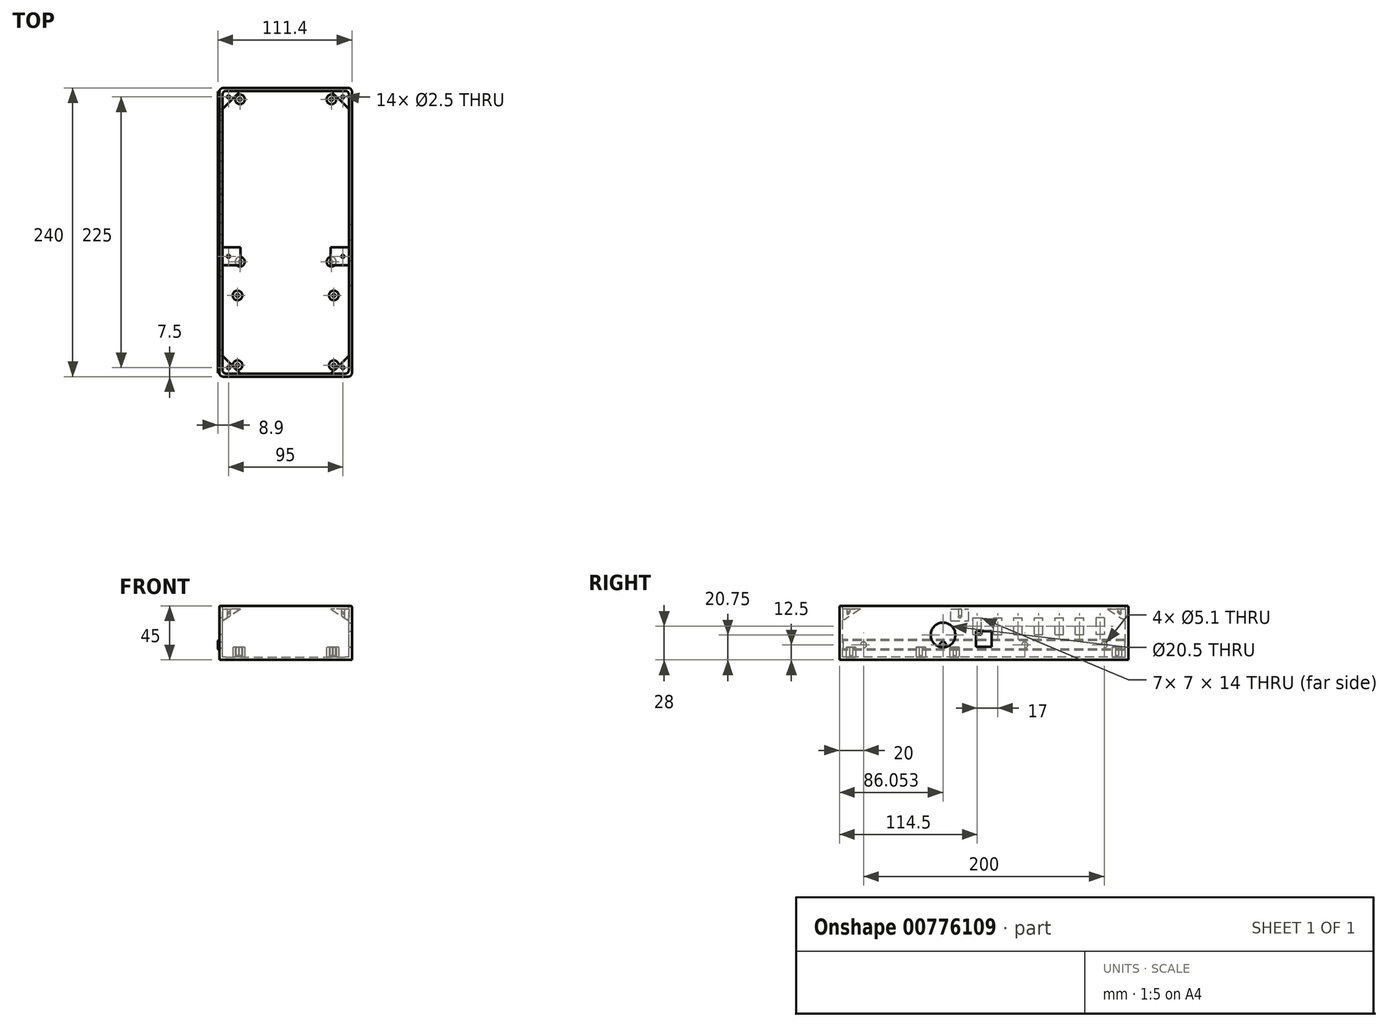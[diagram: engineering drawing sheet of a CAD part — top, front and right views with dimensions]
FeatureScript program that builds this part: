
annotation { "Feature Type Name" : "Feature", "Feature Type Description" : "" }
export const myFeature = defineFeature(function(context is Context, id is Id, definition is map)
    precondition{}
    {
        {
            var Q0;
            Q0=qCreatedBy(makeId("Top.planeOp"),FACE);
            var sketch = newSketch(context, id + "F0", { "sketchPlane" : qUnion([Q0])});
            skLineSegment(sketch, "E0.bottom", {"start": v(55, -120) * mm, "end": v(-55, -120) * mm});
            skLineSegment(sketch, "E0.top", {"start": v(55, 120) * mm, "end": v(-55, 120) * mm});
            skLineSegment(sketch, "E0.left", {"start": v(55, -120) * mm, "end": v(55, 120) * mm});
            skLineSegment(sketch, "E0.right", {"start": v(-55, -120) * mm, "end": v(-55, 120) * mm});
            skPoint(sketch, "E0.middle", {"position": v(0, 0) * mm});
            skSolve(sketch);
        }
        {
            var Q0;
            Q0=makeQuery(id+"F0.imprint","IMPRINT",FACE,{"disambiguationData":[TD([[makeQuery(id+"F0.imprint","IMPRINT",EDGE,{"derivedFrom":sQuery(id+"F0.wireOp",EDGE,"E0.bottom")}),-1.0]])]});
            extrude(context, id + "F1", {"entities" : qUnion([Q0]), "depth" : 45 * mm, "offsetDistance" : 25 * mm});
        }
        {
            var Q0;
            Q0=makeQuery(id+"F1.opExtrude","CAP_FACE",FACE,{"disambiguationData":[OSD([sQuery(id+"F0.wireOp",EDGE,"E0.bottom"),sQuery(id+"F0.wireOp",EDGE,"E0.top"),sQuery(id+"F0.wireOp",EDGE,"E0.left"),sQuery(id+"F0.wireOp",EDGE,"E0.right")])],"isStart":false});
            var sketch = newSketch(context, id + "F2", { "sketchPlane" : qUnion([Q0])});
            skLineSegment(sketch, "E1.bottom", {"start": v(52.5, -117.5) * mm, "end": v(-52.5, -117.5) * mm});
            skLineSegment(sketch, "E1.top", {"start": v(52.5, 117.5) * mm, "end": v(-52.5, 117.5) * mm});
            skLineSegment(sketch, "E1.left", {"start": v(52.5, -117.5) * mm, "end": v(52.5, 117.5) * mm});
            skLineSegment(sketch, "E1.right", {"start": v(-52.5, -117.5) * mm, "end": v(-52.5, 117.5) * mm});
            skPoint(sketch, "E1.middle", {"position": v(0, 0) * mm});
            skSolve(sketch);
        }
        {
            var Q0;
            Q0=qSketchRegion(id+"F2",true);
            var Q1;
            Q1=makeQuery(id+"F1.opExtrude","CAP_FACE",FACE,{"disambiguationData":[OSD([sQuery(id+"F0.wireOp",EDGE,"E0.bottom"),sQuery(id+"F0.wireOp",EDGE,"E0.top"),sQuery(id+"F0.wireOp",EDGE,"E0.left"),sQuery(id+"F0.wireOp",EDGE,"E0.right")])],"isStart":true});
            extrude(context, id + "F3", {"entities" : qUnion([Q0]), "operationType" : NewBodyOperationType.REMOVE, "endBound" : BoundingType.UP_TO_SURFACE, "oppositeDirection" : true, "depth" : 35 * mm, "endBoundEntityFace" : qUnion([Q1]), "hasOffset" : true, "offsetDistance" : 2.5 * mm});
        }
        {
            var Q0;
            Q0=makeQuery(id+"F3.boolean.opBoolean","COPY",FACE,{"derivedFrom":makeQuery(id+"F3.opExtrude","CAP_FACE",FACE,{"disambiguationData":[OSD([sQuery(id+"F2.wireOp",EDGE,"E1.bottom"),sQuery(id+"F2.wireOp",EDGE,"E1.top"),sQuery(id+"F2.wireOp",EDGE,"E1.left"),sQuery(id+"F2.wireOp",EDGE,"E1.right")])],"isStart":false})});
            var sketch = newSketch(context, id + "F4", { "sketchPlane" : qUnion([Q0])});
            skCircle(sketch, "E2", {"center": v(-38, 110.5) * mm, "radius": 4 * mm});
            skCircle(sketch, "E3", {"center": v(38, 110.5) * mm, "radius": 4 * mm});
            skCircle(sketch, "E4", {"center": v(-38, -24.5) * mm, "radius": 4 * mm});
            skCircle(sketch, "E5", {"center": v(38, -24.5) * mm, "radius": 4 * mm});
            skCircle(sketch, "E6", {"center": v(-40, -52.5) * mm, "radius": 4 * mm});
            skCircle(sketch, "E7", {"center": v(40, -52.5) * mm, "radius": 4 * mm});
            skCircle(sketch, "E8", {"center": v(-40, -110.5) * mm, "radius": 4 * mm});
            skCircle(sketch, "E9", {"center": v(40, -110.5) * mm, "radius": 4 * mm});
            skSolve(sketch);
        }
        {
            var Q0;
            Q0=makeQuery(id+"F4.imprint","IMPRINT",FACE,{"disambiguationData":[TD([[makeQuery(id+"F4.imprint","IMPRINT",EDGE,{"derivedFrom":sQuery(id+"F4.wireOp",EDGE,"E2")}),1.0]])]});
            var Q1;
            Q1=makeQuery(id+"F4.imprint","IMPRINT",FACE,{"disambiguationData":[TD([[makeQuery(id+"F4.imprint","IMPRINT",EDGE,{"derivedFrom":sQuery(id+"F4.wireOp",EDGE,"E3")}),1.0]])]});
            var Q2;
            Q2=makeQuery(id+"F4.imprint","IMPRINT",FACE,{"disambiguationData":[TD([[makeQuery(id+"F4.imprint","IMPRINT",EDGE,{"derivedFrom":sQuery(id+"F4.wireOp",EDGE,"E4")}),1.0]])]});
            var Q3;
            Q3=makeQuery(id+"F4.imprint","IMPRINT",FACE,{"disambiguationData":[TD([[makeQuery(id+"F4.imprint","IMPRINT",EDGE,{"derivedFrom":sQuery(id+"F4.wireOp",EDGE,"E5")}),1.0]])]});
            var Q4;
            Q4=makeQuery(id+"F4.imprint","IMPRINT",FACE,{"disambiguationData":[TD([[makeQuery(id+"F4.imprint","IMPRINT",EDGE,{"derivedFrom":sQuery(id+"F4.wireOp",EDGE,"E6")}),1.0]])]});
            var Q5;
            Q5=makeQuery(id+"F4.imprint","IMPRINT",FACE,{"disambiguationData":[TD([[makeQuery(id+"F4.imprint","IMPRINT",EDGE,{"derivedFrom":sQuery(id+"F4.wireOp",EDGE,"E7")}),1.0]])]});
            var Q6;
            Q6=makeQuery(id+"F4.imprint","IMPRINT",FACE,{"disambiguationData":[TD([[makeQuery(id+"F4.imprint","IMPRINT",EDGE,{"derivedFrom":sQuery(id+"F4.wireOp",EDGE,"E8")}),1.0]])]});
            var Q7;
            Q7=makeQuery(id+"F4.imprint","IMPRINT",FACE,{"disambiguationData":[TD([[makeQuery(id+"F4.imprint","IMPRINT",EDGE,{"derivedFrom":sQuery(id+"F4.wireOp",EDGE,"E9")}),1.0]])]});
            extrude(context, id + "F5", {"entities" : qUnion([Q0, Q1, Q2, Q3, Q4, Q5, Q6, Q7]), "operationType" : NewBodyOperationType.ADD, "depth" : 8 * mm, "offsetDistance" : 25 * mm});
        }
        {
            var Q0;
            Q0=makeQuery(id+"F1.opExtrude","SWEPT_FACE",FACE,{"disambiguationData":[OSD([sQuery(id+"F0.wireOp",EDGE,"E0.left")])]});
            var sketch = newSketch(context, id + "F6", { "sketchPlane" : qUnion([Q0])});
            skLineSegment(sketch, "E10.bottom", {"start": v(-6.5, 24) * mm, "end": v(6.5, 24) * mm});
            skLineSegment(sketch, "E10.top", {"start": v(-6.5, 11) * mm, "end": v(6.5, 11) * mm});
            skLineSegment(sketch, "E10.left", {"start": v(-6.5, 24) * mm, "end": v(-6.5, 11) * mm});
            skLineSegment(sketch, "E10.right", {"start": v(6.5, 24) * mm, "end": v(6.5, 11) * mm});
            skPoint(sketch, "E11.0", {"position": v(-24.5, 2.5) * mm});
            skLineSegment(sketch, "E12.0.0", {"start": v(-28.5, 10.5) * mm, "end": v(-20.5, 10.5) * mm});
            skSolve(sketch);
        }
        {
            var Q0;
            Q0=makeQuery(id+"F6.imprint","IMPRINT",FACE,{"disambiguationData":[TD([[makeQuery(id+"F6.imprint","IMPRINT",EDGE,{"derivedFrom":sQuery(id+"F6.wireOp",EDGE,"E10.bottom")}),-1.0]])]});
            var Q1;
            Q1=makeQuery(id+"F3.boolean.opBoolean","COPY",FACE,{"derivedFrom":makeQuery(id+"F3.opExtrude","SWEPT_FACE",FACE,{"disambiguationData":[OSD([sQuery(id+"F2.wireOp",EDGE,"E1.left")])]})});
            extrude(context, id + "F7", {"entities" : qUnion([Q0]), "operationType" : NewBodyOperationType.REMOVE, "endBound" : BoundingType.UP_TO_SURFACE, "oppositeDirection" : true, "depth" : 25 * mm, "endBoundEntityFace" : qUnion([Q1]), "offsetDistance" : 25 * mm});
        }
        {
            var Q0;
            Q0=makeQuery(id+"F1.opExtrude","SWEPT_FACE",FACE,{"disambiguationData":[OSD([sQuery(id+"F0.wireOp",EDGE,"E0.right")])]});
            var sketch = newSketch(context, id + "F8", { "sketchPlane" : qUnion([Q0])});
            skLineSegment(sketch, "E13.bottom", {"start": v(-100, 35) * mm, "end": v(-93, 35) * mm});
            skLineSegment(sketch, "E13.top", {"start": v(-100, 21) * mm, "end": v(-93, 21) * mm});
            skLineSegment(sketch, "E13.left", {"start": v(-100, 35) * mm, "end": v(-100, 21) * mm});
            skLineSegment(sketch, "E13.right", {"start": v(-93, 35) * mm, "end": v(-93, 21) * mm});
            skLineSegment(sketch, "E14.bottom", {"start": v(-76, 21) * mm, "end": v(-83, 21) * mm});
            skLineSegment(sketch, "E14.top", {"start": v(-76, 35) * mm, "end": v(-83, 35) * mm});
            skLineSegment(sketch, "E14.left", {"start": v(-76, 21) * mm, "end": v(-76, 35) * mm});
            skLineSegment(sketch, "E14.right", {"start": v(-83, 21) * mm, "end": v(-83, 35) * mm});
            skPoint(sketch, "E14.middle", {"position": v(-79.5, 28) * mm});
            skLineSegment(sketch, "E15.bottom", {"start": v(-59, 21) * mm, "end": v(-66, 21) * mm});
            skLineSegment(sketch, "E15.top", {"start": v(-59, 35) * mm, "end": v(-66, 35) * mm});
            skLineSegment(sketch, "E15.left", {"start": v(-59, 21) * mm, "end": v(-59, 35) * mm});
            skLineSegment(sketch, "E15.right", {"start": v(-66, 21) * mm, "end": v(-66, 35) * mm});
            skPoint(sketch, "E15.middle", {"position": v(-62.5, 28) * mm});
            skLineSegment(sketch, "E16.bottom", {"start": v(-42, 21) * mm, "end": v(-49, 21) * mm});
            skLineSegment(sketch, "E16.top", {"start": v(-42, 35) * mm, "end": v(-49, 35) * mm});
            skLineSegment(sketch, "E16.left", {"start": v(-42, 21) * mm, "end": v(-42, 35) * mm});
            skLineSegment(sketch, "E16.right", {"start": v(-49, 21) * mm, "end": v(-49, 35) * mm});
            skPoint(sketch, "E16.middle", {"position": v(-45.5, 28) * mm});
            skLineSegment(sketch, "E17.bottom", {"start": v(9, 21) * mm, "end": v(2, 21) * mm});
            skLineSegment(sketch, "E17.top", {"start": v(9, 35) * mm, "end": v(2, 35) * mm});
            skLineSegment(sketch, "E17.left", {"start": v(9, 21) * mm, "end": v(9, 35) * mm});
            skLineSegment(sketch, "E17.right", {"start": v(2, 21) * mm, "end": v(2, 35) * mm});
            skPoint(sketch, "E17.middle", {"position": v(5.5, 28) * mm});
            skLineSegment(sketch, "E18.bottom", {"start": v(-8, 21) * mm, "end": v(-15, 21) * mm});
            skLineSegment(sketch, "E18.top", {"start": v(-8, 35) * mm, "end": v(-15, 35) * mm});
            skLineSegment(sketch, "E18.left", {"start": v(-8, 21) * mm, "end": v(-8, 35) * mm});
            skLineSegment(sketch, "E18.right", {"start": v(-15, 21) * mm, "end": v(-15, 35) * mm});
            skPoint(sketch, "E18.middle", {"position": v(-11.5, 28) * mm});
            skLineSegment(sketch, "E19.bottom", {"start": v(-25, 21) * mm, "end": v(-32, 21) * mm});
            skLineSegment(sketch, "E19.top", {"start": v(-25, 35) * mm, "end": v(-32, 35) * mm});
            skLineSegment(sketch, "E19.left", {"start": v(-25, 21) * mm, "end": v(-25, 35) * mm});
            skLineSegment(sketch, "E19.right", {"start": v(-32, 21) * mm, "end": v(-32, 35) * mm});
            skPoint(sketch, "E19.middle", {"position": v(-28.5, 28) * mm});
            skSolve(sketch);
        }
        {
            var Q0;
            Q0=makeQuery(id+"F8.imprint","IMPRINT",FACE,{"disambiguationData":[TD([[makeQuery(id+"F8.imprint","IMPRINT",EDGE,{"derivedFrom":sQuery(id+"F8.wireOp",EDGE,"E15.bottom")}),-1.0]])]});
            var Q1;
            Q1=makeQuery(id+"F8.imprint","IMPRINT",FACE,{"disambiguationData":[TD([[makeQuery(id+"F8.imprint","IMPRINT",EDGE,{"derivedFrom":sQuery(id+"F8.wireOp",EDGE,"E16.bottom")}),-1.0]])]});
            var Q2;
            Q2=makeQuery(id+"F8.imprint","IMPRINT",FACE,{"disambiguationData":[TD([[makeQuery(id+"F8.imprint","IMPRINT",EDGE,{"derivedFrom":sQuery(id+"F8.wireOp",EDGE,"E19.bottom")}),-1.0]])]});
            var Q3;
            Q3=makeQuery(id+"F8.imprint","IMPRINT",FACE,{"disambiguationData":[TD([[makeQuery(id+"F8.imprint","IMPRINT",EDGE,{"derivedFrom":sQuery(id+"F8.wireOp",EDGE,"E18.bottom")}),-1.0]])]});
            var Q4;
            Q4=makeQuery(id+"F8.imprint","IMPRINT",FACE,{"disambiguationData":[TD([[makeQuery(id+"F8.imprint","IMPRINT",EDGE,{"derivedFrom":sQuery(id+"F8.wireOp",EDGE,"E17.bottom")}),-1.0]])]});
            var Q5;
            Q5=makeQuery(id+"F8.imprint","IMPRINT",FACE,{"disambiguationData":[TD([[makeQuery(id+"F8.imprint","IMPRINT",EDGE,{"derivedFrom":sQuery(id+"F8.wireOp",EDGE,"E14.bottom")}),-1.0]])]});
            var Q6;
            Q6=makeQuery(id+"F8.imprint","IMPRINT",FACE,{"disambiguationData":[TD([[makeQuery(id+"F8.imprint","IMPRINT",EDGE,{"derivedFrom":sQuery(id+"F8.wireOp",EDGE,"E13.bottom")}),-1.0]])]});
            var Q7;
            Q7=makeQuery(id+"F3.boolean.opBoolean","COPY",FACE,{"derivedFrom":makeQuery(id+"F3.opExtrude","SWEPT_FACE",FACE,{"disambiguationData":[OSD([sQuery(id+"F2.wireOp",EDGE,"E1.right")])]})});
            extrude(context, id + "F9", {"entities" : qUnion([Q0, Q1, Q2, Q3, Q4, Q5, Q6]), "operationType" : NewBodyOperationType.REMOVE, "endBound" : BoundingType.UP_TO_SURFACE, "oppositeDirection" : true, "depth" : 25 * mm, "endBoundEntityFace" : qUnion([Q7]), "offsetDistance" : 25 * mm});
        }
        {
            var Q0;
            Q0=makeQuery(id+"F1.opExtrude","SWEPT_EDGE",EDGE,{"disambiguationData":[OSD([sQuery(id+"F0.wireOp",EDGE,"E0.bottom"),sQuery(id+"F0.wireOp",EDGE,"E0.right")])]});
            var Q1;
            Q1=makeQuery(id+"F1.opExtrude","SWEPT_EDGE",EDGE,{"disambiguationData":[OSD([sQuery(id+"F0.wireOp",EDGE,"E0.bottom"),sQuery(id+"F0.wireOp",EDGE,"E0.left")])]});
            var Q2;
            Q2=makeQuery(id+"F1.opExtrude","SWEPT_EDGE",EDGE,{"disambiguationData":[OSD([sQuery(id+"F0.wireOp",EDGE,"E0.top"),sQuery(id+"F0.wireOp",EDGE,"E0.right")])]});
            var Q3;
            Q3=makeQuery(id+"F1.opExtrude","SWEPT_EDGE",EDGE,{"disambiguationData":[OSD([sQuery(id+"F0.wireOp",EDGE,"E0.top"),sQuery(id+"F0.wireOp",EDGE,"E0.left")])]});
            fillet(context, id + "F10", {"entities" : qUnion([Q0, Q1, Q2, Q3]), "radius" : 3 * mm, "tangentPropagation" : true, "allowEdgeOverflow" : false});
        }
        {
            var Q0;
            Q0=makeQuery(id+"F3.boolean.opBoolean","COPY",EDGE,{"derivedFrom":makeQuery(id+"F3.opExtrude","SWEPT_EDGE",EDGE,{"disambiguationData":[OSD([sQuery(id+"F2.wireOp",EDGE,"E1.bottom"),sQuery(id+"F2.wireOp",EDGE,"E1.right")])]})});
            var Q1;
            Q1=makeQuery(id+"F3.boolean.opBoolean","COPY",EDGE,{"derivedFrom":makeQuery(id+"F3.opExtrude","SWEPT_EDGE",EDGE,{"disambiguationData":[OSD([sQuery(id+"F2.wireOp",EDGE,"E1.bottom"),sQuery(id+"F2.wireOp",EDGE,"E1.left")])]})});
            var Q2;
            Q2=makeQuery(id+"F3.boolean.opBoolean","COPY",EDGE,{"derivedFrom":makeQuery(id+"F3.opExtrude","SWEPT_EDGE",EDGE,{"disambiguationData":[OSD([sQuery(id+"F2.wireOp",EDGE,"E1.top"),sQuery(id+"F2.wireOp",EDGE,"E1.right")])]})});
            var Q3;
            Q3=makeQuery(id+"F3.boolean.opBoolean","COPY",EDGE,{"derivedFrom":makeQuery(id+"F3.opExtrude","SWEPT_EDGE",EDGE,{"disambiguationData":[OSD([sQuery(id+"F2.wireOp",EDGE,"E1.top"),sQuery(id+"F2.wireOp",EDGE,"E1.left")])]})});
            fillet(context, id + "F11", {"entities" : qUnion([Q0, Q1, Q2, Q3]), "radius" : 3 * mm, "tangentPropagation" : true, "allowEdgeOverflow" : false});
        }
        {
            var Q0;
            Q0=makeQuery(id+"F1.opExtrude","SWEPT_FACE",FACE,{"disambiguationData":[OSD([sQuery(id+"F0.wireOp",EDGE,"E0.left")])]});
            var sketch = newSketch(context, id + "F12", { "sketchPlane" : qUnion([Q0])});
            skCircle(sketch, "E20", {"center": v(-33.95, 20.75) * mm, "radius": 10.25 * mm});
            skLineSegment(sketch, "E21.0", {"start": v(-56.5, 10.5) * mm, "end": v(-48.5, 10.5) * mm});
            skLineSegment(sketch, "E22", {"start": v(-52.5, 10.5) * mm, "end": v(-13.25, 10.5) * mm});
            skSolve(sketch);
        }
        {
            var Q0;
            Q0=makeQuery(id+"F12.imprint","IMPRINT",FACE,{"disambiguationData":[TD([[makeQuery(id+"F12.imprint","IMPRINT",EDGE,{"derivedFrom":sQuery(id+"F12.wireOp",EDGE,"E20")}),1.0]])]});
            var Q1;
            Q1=makeQuery(id+"F3.boolean.opBoolean","COPY",FACE,{"derivedFrom":makeQuery(id+"F3.opExtrude","SWEPT_FACE",FACE,{"disambiguationData":[OSD([sQuery(id+"F2.wireOp",EDGE,"E1.left")])]})});
            extrude(context, id + "F13", {"entities" : qUnion([Q0]), "operationType" : NewBodyOperationType.REMOVE, "endBound" : BoundingType.UP_TO_SURFACE, "oppositeDirection" : true, "depth" : 25 * mm, "endBoundEntityFace" : qUnion([Q1]), "offsetDistance" : 25 * mm});
        }
        {
            var Q0;
            Q0=makeQuery(id+"F1.opExtrude","CAP_EDGE",EDGE,{"disambiguationData":[OSD([sQuery(id+"F0.wireOp",EDGE,"E0.bottom")])],"isStart":false});
            var Q1;
            Q1=makeQuery(id+"F13.boolean.opBoolean","COPY",EDGE,{"derivedFrom":makeQuery(id+"F13.opExtrude","CAP_EDGE",EDGE,{"disambiguationData":[OSD([sQuery(id+"F12.wireOp",EDGE,"E20")])],"isStart":true})});
            var Q2;
            Q2=makeQuery(id+"F7.boolean.opBoolean","COPY",EDGE,{"derivedFrom":makeQuery(id+"F7.opExtrude","CAP_EDGE",EDGE,{"disambiguationData":[OSD([sQuery(id+"F6.wireOp",EDGE,"E10.left")])],"isStart":true})});
            var Q3;
            Q3=makeQuery(id+"F7.boolean.opBoolean","COPY",EDGE,{"derivedFrom":makeQuery(id+"F7.opExtrude","CAP_EDGE",EDGE,{"disambiguationData":[OSD([sQuery(id+"F6.wireOp",EDGE,"E10.top")])],"isStart":true})});
            var Q4;
            Q4=makeQuery(id+"F7.boolean.opBoolean","COPY",EDGE,{"derivedFrom":makeQuery(id+"F7.opExtrude","CAP_EDGE",EDGE,{"disambiguationData":[OSD([sQuery(id+"F6.wireOp",EDGE,"E10.right")])],"isStart":true})});
            var Q5;
            Q5=makeQuery(id+"F7.boolean.opBoolean","COPY",EDGE,{"derivedFrom":makeQuery(id+"F7.opExtrude","CAP_EDGE",EDGE,{"disambiguationData":[OSD([sQuery(id+"F6.wireOp",EDGE,"E10.bottom")])],"isStart":true})});
            var Q6;
            Q6=makeQuery(id+"F9.boolean.opBoolean","COPY",EDGE,{"derivedFrom":makeQuery(id+"F9.opExtrude","CAP_EDGE",EDGE,{"disambiguationData":[OSD([sQuery(id+"F8.wireOp",EDGE,"E13.left")])],"isStart":true})});
            var Q7;
            Q7=makeQuery(id+"F9.boolean.opBoolean","COPY",EDGE,{"derivedFrom":makeQuery(id+"F9.opExtrude","CAP_EDGE",EDGE,{"disambiguationData":[OSD([sQuery(id+"F8.wireOp",EDGE,"E13.right")])],"isStart":true})});
            var Q8;
            Q8=makeQuery(id+"F9.boolean.opBoolean","COPY",EDGE,{"derivedFrom":makeQuery(id+"F9.opExtrude","CAP_EDGE",EDGE,{"disambiguationData":[OSD([sQuery(id+"F8.wireOp",EDGE,"E13.top")])],"isStart":true})});
            var Q9;
            Q9=makeQuery(id+"F9.boolean.opBoolean","COPY",EDGE,{"derivedFrom":makeQuery(id+"F9.opExtrude","CAP_EDGE",EDGE,{"disambiguationData":[OSD([sQuery(id+"F8.wireOp",EDGE,"E13.bottom")])],"isStart":true})});
            var Q10;
            Q10=makeQuery(id+"F9.boolean.opBoolean","COPY",EDGE,{"derivedFrom":makeQuery(id+"F9.opExtrude","CAP_EDGE",EDGE,{"disambiguationData":[OSD([sQuery(id+"F8.wireOp",EDGE,"E14.top")])],"isStart":true})});
            var Q11;
            Q11=makeQuery(id+"F9.boolean.opBoolean","COPY",EDGE,{"derivedFrom":makeQuery(id+"F9.opExtrude","CAP_EDGE",EDGE,{"disambiguationData":[OSD([sQuery(id+"F8.wireOp",EDGE,"E14.right")])],"isStart":true})});
            var Q12;
            Q12=makeQuery(id+"F9.boolean.opBoolean","COPY",EDGE,{"derivedFrom":makeQuery(id+"F9.opExtrude","CAP_EDGE",EDGE,{"disambiguationData":[OSD([sQuery(id+"F8.wireOp",EDGE,"E14.bottom")])],"isStart":true})});
            var Q13;
            Q13=makeQuery(id+"F9.boolean.opBoolean","COPY",EDGE,{"derivedFrom":makeQuery(id+"F9.opExtrude","CAP_EDGE",EDGE,{"disambiguationData":[OSD([sQuery(id+"F8.wireOp",EDGE,"E14.left")])],"isStart":true})});
            var Q14;
            Q14=makeQuery(id+"F9.boolean.opBoolean","COPY",EDGE,{"derivedFrom":makeQuery(id+"F9.opExtrude","CAP_EDGE",EDGE,{"disambiguationData":[OSD([sQuery(id+"F8.wireOp",EDGE,"E15.top")])],"isStart":true})});
            var Q15;
            Q15=makeQuery(id+"F9.boolean.opBoolean","COPY",EDGE,{"derivedFrom":makeQuery(id+"F9.opExtrude","CAP_EDGE",EDGE,{"disambiguationData":[OSD([sQuery(id+"F8.wireOp",EDGE,"E15.right")])],"isStart":true})});
            var Q16;
            Q16=makeQuery(id+"F9.boolean.opBoolean","COPY",EDGE,{"derivedFrom":makeQuery(id+"F9.opExtrude","CAP_EDGE",EDGE,{"disambiguationData":[OSD([sQuery(id+"F8.wireOp",EDGE,"E15.bottom")])],"isStart":true})});
            var Q17;
            Q17=makeQuery(id+"F9.boolean.opBoolean","COPY",EDGE,{"derivedFrom":makeQuery(id+"F9.opExtrude","CAP_EDGE",EDGE,{"disambiguationData":[OSD([sQuery(id+"F8.wireOp",EDGE,"E15.left")])],"isStart":true})});
            var Q18;
            Q18=makeQuery(id+"F9.boolean.opBoolean","COPY",EDGE,{"derivedFrom":makeQuery(id+"F9.opExtrude","CAP_EDGE",EDGE,{"disambiguationData":[OSD([sQuery(id+"F8.wireOp",EDGE,"E16.top")])],"isStart":true})});
            var Q19;
            Q19=makeQuery(id+"F9.boolean.opBoolean","COPY",EDGE,{"derivedFrom":makeQuery(id+"F9.opExtrude","CAP_EDGE",EDGE,{"disambiguationData":[OSD([sQuery(id+"F8.wireOp",EDGE,"E16.left")])],"isStart":true})});
            var Q20;
            Q20=makeQuery(id+"F9.boolean.opBoolean","COPY",EDGE,{"derivedFrom":makeQuery(id+"F9.opExtrude","CAP_EDGE",EDGE,{"disambiguationData":[OSD([sQuery(id+"F8.wireOp",EDGE,"E16.right")])],"isStart":true})});
            var Q21;
            Q21=makeQuery(id+"F9.boolean.opBoolean","COPY",EDGE,{"derivedFrom":makeQuery(id+"F9.opExtrude","CAP_EDGE",EDGE,{"disambiguationData":[OSD([sQuery(id+"F8.wireOp",EDGE,"E16.bottom")])],"isStart":true})});
            var Q22;
            Q22=makeQuery(id+"F9.boolean.opBoolean","COPY",EDGE,{"derivedFrom":makeQuery(id+"F9.opExtrude","CAP_EDGE",EDGE,{"disambiguationData":[OSD([sQuery(id+"F8.wireOp",EDGE,"E19.right")])],"isStart":true})});
            var Q23;
            Q23=makeQuery(id+"F9.boolean.opBoolean","COPY",EDGE,{"derivedFrom":makeQuery(id+"F9.opExtrude","CAP_EDGE",EDGE,{"disambiguationData":[OSD([sQuery(id+"F8.wireOp",EDGE,"E19.bottom")])],"isStart":true})});
            var Q24;
            Q24=makeQuery(id+"F9.boolean.opBoolean","COPY",EDGE,{"derivedFrom":makeQuery(id+"F9.opExtrude","CAP_EDGE",EDGE,{"disambiguationData":[OSD([sQuery(id+"F8.wireOp",EDGE,"E19.top")])],"isStart":true})});
            var Q25;
            Q25=makeQuery(id+"F9.boolean.opBoolean","COPY",EDGE,{"derivedFrom":makeQuery(id+"F9.opExtrude","CAP_EDGE",EDGE,{"disambiguationData":[OSD([sQuery(id+"F8.wireOp",EDGE,"E19.left")])],"isStart":true})});
            var Q26;
            Q26=makeQuery(id+"F9.boolean.opBoolean","COPY",EDGE,{"derivedFrom":makeQuery(id+"F9.opExtrude","CAP_EDGE",EDGE,{"disambiguationData":[OSD([sQuery(id+"F8.wireOp",EDGE,"E18.right")])],"isStart":true})});
            var Q27;
            Q27=makeQuery(id+"F9.boolean.opBoolean","COPY",EDGE,{"derivedFrom":makeQuery(id+"F9.opExtrude","CAP_EDGE",EDGE,{"disambiguationData":[OSD([sQuery(id+"F8.wireOp",EDGE,"E18.bottom")])],"isStart":true})});
            var Q28;
            Q28=makeQuery(id+"F9.boolean.opBoolean","COPY",EDGE,{"derivedFrom":makeQuery(id+"F9.opExtrude","CAP_EDGE",EDGE,{"disambiguationData":[OSD([sQuery(id+"F8.wireOp",EDGE,"E18.top")])],"isStart":true})});
            var Q29;
            Q29=makeQuery(id+"F9.boolean.opBoolean","COPY",EDGE,{"derivedFrom":makeQuery(id+"F9.opExtrude","CAP_EDGE",EDGE,{"disambiguationData":[OSD([sQuery(id+"F8.wireOp",EDGE,"E18.left")])],"isStart":true})});
            var Q30;
            Q30=makeQuery(id+"F9.boolean.opBoolean","COPY",EDGE,{"derivedFrom":makeQuery(id+"F9.opExtrude","CAP_EDGE",EDGE,{"disambiguationData":[OSD([sQuery(id+"F8.wireOp",EDGE,"E17.top")])],"isStart":true})});
            var Q31;
            Q31=makeQuery(id+"F9.boolean.opBoolean","COPY",EDGE,{"derivedFrom":makeQuery(id+"F9.opExtrude","CAP_EDGE",EDGE,{"disambiguationData":[OSD([sQuery(id+"F8.wireOp",EDGE,"E17.right")])],"isStart":true})});
            var Q32;
            Q32=makeQuery(id+"F9.boolean.opBoolean","COPY",EDGE,{"derivedFrom":makeQuery(id+"F9.opExtrude","CAP_EDGE",EDGE,{"disambiguationData":[OSD([sQuery(id+"F8.wireOp",EDGE,"E17.left")])],"isStart":true})});
            var Q33;
            Q33=makeQuery(id+"F9.boolean.opBoolean","COPY",EDGE,{"derivedFrom":makeQuery(id+"F9.opExtrude","CAP_EDGE",EDGE,{"disambiguationData":[OSD([sQuery(id+"F8.wireOp",EDGE,"E17.bottom")])],"isStart":true})});
            fillet(context, id + "F14", {"entities" : qUnion([Q0, Q1, Q2, Q3, Q4, Q5, Q6, Q7, Q8, Q9, Q10, Q11, Q12, Q13, Q14, Q15, Q16, Q17, Q18, Q19, Q20, Q21, Q22, Q23, Q24, Q25, Q26, Q27, Q28, Q29, Q30, Q31, Q32, Q33]), "radius" : 1 * mm, "tangentPropagation" : true, "allowEdgeOverflow" : false});
        }
        {
            var Q0;
            Q0=makeQuery(id+"F1.opExtrude","CAP_FACE",FACE,{"disambiguationData":[OSD([sQuery(id+"F0.wireOp",EDGE,"E0.bottom"),sQuery(id+"F0.wireOp",EDGE,"E0.top"),sQuery(id+"F0.wireOp",EDGE,"E0.left"),sQuery(id+"F0.wireOp",EDGE,"E0.right")])],"isStart":false});
            cPlane(context, id + "F15", {"entities" : qUnion([Q0]), "cplaneType" : CPlaneType.OFFSET, "offset" : 2.5 * mm, "oppositeDirection" : true, "width" : 150 * mm, "height" : 150 * mm});
        }
        {
            var Q0;
            Q0=qCreatedBy(id+"F15.planeOp",FACE);
            cPlane(context, id + "F16", {"entities" : qUnion([Q0]), "cplaneType" : CPlaneType.OFFSET, "offset" : 10 * mm, "oppositeDirection" : true, "width" : 150 * mm, "height" : 150 * mm});
        }
        {
            var Q0;
            Q0=qCreatedBy(id+"F15.planeOp",FACE);
            var sketch = newSketch(context, id + "F17", { "sketchPlane" : qUnion([Q0])});
            skLineSegment(sketch, "E23.bottom", {"start": v(52.5, -117.5) * mm, "end": v(-52.5, -117.5) * mm});
            skLineSegment(sketch, "E23.top", {"start": v(52.5, 117.5) * mm, "end": v(-52.5, 117.5) * mm});
            skLineSegment(sketch, "E23.left", {"start": v(52.5, -117.5) * mm, "end": v(52.5, 117.5) * mm});
            skLineSegment(sketch, "E23.right", {"start": v(-52.5, -117.5) * mm, "end": v(-52.5, 117.5) * mm});
            skPoint(sketch, "E23.middle", {"position": v(0, 0) * mm});
            skLineSegment(sketch, "E24", {"start": v(-52.5, 117.5) * mm, "end": v(-37.5, 117.5) * mm});
            skLineSegment(sketch, "E25", {"start": v(-37.5, 117.5) * mm, "end": v(-52.5, 102.5) * mm});
            skLineSegment(sketch, "E26", {"start": v(-52.5, 102.5) * mm, "end": v(-52.5, 117.5) * mm});
            skPoint(sketch, "E27", {"position": v(-47.5, 112.5) * mm});
            skLineSegment(sketch, "E28", {"start": v(52.5, 117.5) * mm, "end": v(52.5, 102.5) * mm});
            skLineSegment(sketch, "E29", {"start": v(52.5, 102.5) * mm, "end": v(37.5, 117.5) * mm});
            skLineSegment(sketch, "E30", {"start": v(37.5, 117.5) * mm, "end": v(52.5, 117.5) * mm});
            skPoint(sketch, "E31", {"position": v(47.5, 112.5) * mm});
            skLineSegment(sketch, "E32", {"start": v(52.5, -117.5) * mm, "end": v(52.5, -102.5) * mm});
            skLineSegment(sketch, "E33", {"start": v(52.5, -102.5) * mm, "end": v(37.5, -117.5) * mm});
            skLineSegment(sketch, "E34", {"start": v(37.5, -117.5) * mm, "end": v(52.5, -117.5) * mm});
            skLineSegment(sketch, "E35", {"start": v(-52.5, -117.5) * mm, "end": v(-52.5, -102.5) * mm});
            skLineSegment(sketch, "E36", {"start": v(-52.5, -102.5) * mm, "end": v(-37.5, -117.5) * mm});
            skLineSegment(sketch, "E37", {"start": v(-37.5, -117.5) * mm, "end": v(-52.5, -117.5) * mm});
            skPoint(sketch, "E38", {"position": v(-47.5, -112.5) * mm});
            skPoint(sketch, "E39", {"position": v(47.5, -112.5) * mm});
            skLineSegment(sketch, "E40", {"start": v(-52.5, -102.5) * mm, "end": v(-52.5, -27.5) * mm, "construction": true});
            skLineSegment(sketch, "E41.bottom", {"start": v(-52.5, -27.5) * mm, "end": v(-37.5, -27.5) * mm});
            skLineSegment(sketch, "E41.top", {"start": v(-52.5, -12.5) * mm, "end": v(-37.5, -12.5) * mm});
            skLineSegment(sketch, "E41.left", {"start": v(-52.5, -27.5) * mm, "end": v(-52.5, -12.5) * mm});
            skLineSegment(sketch, "E41.right", {"start": v(-37.5, -27.5) * mm, "end": v(-37.5, -12.5) * mm});
            skLineSegment(sketch, "E42", {"start": v(52.5, -102.5) * mm, "end": v(52.5, -27.5) * mm, "construction": true});
            skLineSegment(sketch, "E43.bottom", {"start": v(52.5, -27.5) * mm, "end": v(37.5, -27.5) * mm});
            skLineSegment(sketch, "E43.top", {"start": v(52.5, -12.5) * mm, "end": v(37.5, -12.5) * mm});
            skLineSegment(sketch, "E43.left", {"start": v(52.5, -27.5) * mm, "end": v(52.5, -12.5) * mm});
            skLineSegment(sketch, "E43.right", {"start": v(37.5, -27.5) * mm, "end": v(37.5, -12.5) * mm});
            skPoint(sketch, "E44.positionSnap0", {"position": v(37.5, -20) * mm});
            skPoint(sketch, "E44.positionSnap1", {"position": v(45, -27.5) * mm});
            skPoint(sketch, "E45.positionSnap0", {"position": v(-45, -27.5) * mm});
            skPoint(sketch, "E45.positionSnap1", {"position": v(-37.5, -20) * mm});
            skPoint(sketch, "E46", {"position": v(-47.5, -20) * mm});
            skPoint(sketch, "E46.positionSnap0", {"position": v(-52.5, -20) * mm});
            skPoint(sketch, "E47", {"position": v(47.5, -20) * mm});
            skPoint(sketch, "E47.positionSnap0", {"position": v(52.5, -20) * mm});
            skSolve(sketch);
        }
        {
            var Q0;
            Q0=qCreatedBy(id+"F16.planeOp",FACE);
            var sketch = newSketch(context, id + "F18", { "sketchPlane" : qUnion([Q0])});
            skLineSegment(sketch, "E48.bottom", {"start": v(52.5, -117.5) * mm, "end": v(-52.5, -117.5) * mm});
            skLineSegment(sketch, "E48.top", {"start": v(52.5, 117.5) * mm, "end": v(-52.5, 117.5) * mm});
            skLineSegment(sketch, "E48.left", {"start": v(52.5, -117.5) * mm, "end": v(52.5, 117.5) * mm});
            skLineSegment(sketch, "E48.right", {"start": v(-52.5, -117.5) * mm, "end": v(-52.5, 117.5) * mm});
            skPoint(sketch, "E48.middle", {"position": v(0, 0) * mm});
            skSolve(sketch);
        }
        {
            var Q1;
            {var subQ3=sQuery(id+"F17.wireOp",EDGE,"E25");Q1=makeQuery(id+"F17.imprint","IMPRINT",FACE,{"disambiguationData":[TD([[makeQuery(id+"F17.imprint","IMPRINT",EDGE,{"derivedFrom":subQ3}),-1.0]])]});}
            var Q2;
            Q2=sQuery(id+"F18.wireOp",VERTEX,"E48.top.end");
            loft(context, id + "F19", {"operationType" : NewBodyOperationType.ADD, "sheetProfilesArray" : [{ "sheetProfileEntities" : qUnion([Q1]) }, { "sheetProfileEntities" : qUnion([Q2]) }]});
        }
        {
            var Q1;
            {var subQ0=sQuery(id+"F17.wireOp",EDGE,"E29");Q1=makeQuery(id+"F17.imprint","IMPRINT",FACE,{"disambiguationData":[TD([[makeQuery(id+"F17.imprint","IMPRINT",EDGE,{"derivedFrom":subQ0}),-1.0]])]});}
            var Q2;
            Q2=sQuery(id+"F18.wireOp",VERTEX,"E48.top.start");
            loft(context, id + "F20", {"operationType" : NewBodyOperationType.ADD, "sheetProfilesArray" : [{ "sheetProfileEntities" : qUnion([Q1]) }, { "sheetProfileEntities" : qUnion([Q2]) }]});
        }
        {
            var Q1;
            {var subQ0=sQuery(id+"F17.wireOp",EDGE,"E33");Q1=makeQuery(id+"F17.imprint","IMPRINT",FACE,{"disambiguationData":[TD([[makeQuery(id+"F17.imprint","IMPRINT",EDGE,{"derivedFrom":subQ0}),1.0]])]});}
            var Q2;
            Q2=sQuery(id+"F18.wireOp",VERTEX,"E48.bottom.start");
            loft(context, id + "F21", {"operationType" : NewBodyOperationType.ADD, "sheetProfilesArray" : [{ "sheetProfileEntities" : qUnion([Q1]) }, { "sheetProfileEntities" : qUnion([Q2]) }]});
        }
        {
            var Q1;
            {var subQ0=sQuery(id+"F17.wireOp",EDGE,"E36");Q1=makeQuery(id+"F17.imprint","IMPRINT",FACE,{"disambiguationData":[TD([[makeQuery(id+"F17.imprint","IMPRINT",EDGE,{"derivedFrom":subQ0}),-1.0]])]});}
            var Q2;
            Q2=sQuery(id+"F18.wireOp",VERTEX,"E48.bottom.end");
            loft(context, id + "F22", {"operationType" : NewBodyOperationType.ADD, "sheetProfilesArray" : [{ "sheetProfileEntities" : qUnion([Q1]) }, { "sheetProfileEntities" : qUnion([Q2]) }]});
        }
        {
            var Q0;
            Q0=sQuery(id+"F17.wireOp",VERTEX,"E38");
            var Q1;
            Q1=sQuery(id+"F17.wireOp",VERTEX,"E27");
            var Q2;
            Q2=sQuery(id+"F17.wireOp",VERTEX,"E31");
            var Q3;
            Q3=sQuery(id+"F17.wireOp",VERTEX,"E39");
            var Q4;
            Q4=makeQuery(id+"F1.opExtrude","SWEPT_BODY",BODY,{"disambiguationData":[OSD([sQuery(id+"F0.wireOp",EDGE,"E0.bottom"),sQuery(id+"F0.wireOp",EDGE,"E0.top"),sQuery(id+"F0.wireOp",EDGE,"E0.left"),sQuery(id+"F0.wireOp",EDGE,"E0.right")])]});
            hole(context, id + "F23", {"style" : HoleStyle.SIMPLE, "endStyle" : HoleEndStyle.BLIND, "holeDiameter" : 2.5 * mm, "majorDiameter" : 5 * mm, "holeDepth" : 10 * mm, "isTappedThrough" : true, "tappedDepth" : 12 * mm, "tapClearance" : 3, "locations" : qUnion([Q0, Q1, Q2, Q3]), "scope" : qUnion([Q4])});
        }
        {
            var Q0;
            Q0=makeQuery(id+"F1.opExtrude","SWEPT_FACE",FACE,{"disambiguationData":[OSD([sQuery(id+"F0.wireOp",EDGE,"E0.right")])]});
            var sketch = newSketch(context, id + "F24", { "sketchPlane" : qUnion([Q0])});
            skLineSegment(sketch, "E49.bottom", {"start": v(-117, 8) * mm, "end": v(117, 8) * mm});
            skLineSegment(sketch, "E49.top", {"start": v(-117, 17) * mm, "end": v(117, 17) * mm});
            skLineSegment(sketch, "E49.left", {"start": v(-117, 8) * mm, "end": v(-117, 17) * mm});
            skLineSegment(sketch, "E49.right", {"start": v(117, 8) * mm, "end": v(117, 17) * mm});
            skSolve(sketch);
        }
        {
            var Q0;
            Q0=makeQuery(id+"F24.imprint","IMPRINT",FACE,{"disambiguationData":[TD([[makeQuery(id+"F24.imprint","IMPRINT",EDGE,{"derivedFrom":sQuery(id+"F24.wireOp",EDGE,"E49.bottom")}),1.0]])]});
            extrude(context, id + "F25", {"entities" : qUnion([Q0]), "operationType" : NewBodyOperationType.ADD, "depth" : 1.4 * mm, "offsetDistance" : 25 * mm});
        }
        {
            var Q0;
            Q0=makeQuery(id+"F25.opExtrude","SWEPT_FACE",FACE,{"disambiguationData":[OSD([sQuery(id+"F24.wireOp",EDGE,"E49.right")])]});
            var sketch = newSketch(context, id + "F26", { "sketchPlane" : qUnion([Q0])});
            skLineSegment(sketch, "E50", {"start": v(-56.4, 12.5) * mm, "end": v(-56.4, 9) * mm, "construction": true});
            skLineSegment(sketch, "E51", {"start": v(-56.4, 12.5) * mm, "end": v(-56.4, 16) * mm, "construction": true});
            skLineSegment(sketch, "E52", {"start": v(-55, 8) * mm, "end": v(-56.4, 9) * mm});
            skLineSegment(sketch, "E53", {"start": v(-56.4, 8) * mm, "end": v(-55, 8) * mm});
            skLineSegment(sketch, "E54", {"start": v(-56.4, 16) * mm, "end": v(-55, 17) * mm});
            skLineSegment(sketch, "E55", {"start": v(-55, 17) * mm, "end": v(-56.4, 17) * mm});
            skLineSegment(sketch, "E56", {"start": v(-56.4, 17) * mm, "end": v(-56.4, 16) * mm});
            skSolve(sketch);
        }
        {
            var Q0;
            Q0=makeQuery(id+"F26.imprint","IMPRINT",FACE,{"disambiguationData":[TD([[makeQuery(id+"F26.imprint","IMPRINT",EDGE,{"derivedFrom":sQuery(id+"F26.wireOp",EDGE,"E54")}),1.0]])]});
            var Q1;
            {var subQ0=sQuery(id+"F26.wireOp",EDGE,"E52");Q1=makeQuery(id+"F26.imprint","IMPRINT",FACE,{"disambiguationData":[TD([[makeQuery(id+"F26.imprint","IMPRINT",EDGE,{"derivedFrom":subQ0}),1.0]])]});}
            var Q2;
            Q2=makeQuery(id+"F25.opExtrude","SWEPT_FACE",FACE,{"disambiguationData":[OSD([sQuery(id+"F24.wireOp",EDGE,"E49.left")])]});
            extrude(context, id + "F27", {"entities" : qUnion([Q0, Q1]), "operationType" : NewBodyOperationType.REMOVE, "endBound" : BoundingType.UP_TO_SURFACE, "oppositeDirection" : true, "depth" : 25 * mm, "endBoundEntityFace" : qUnion([Q2]), "offsetDistance" : 25 * mm});
        }
        {
            var Q0;
            Q0=makeQuery(id+"F25.opExtrude","CAP_FACE",FACE,{"disambiguationData":[OSD([sQuery(id+"F24.wireOp",EDGE,"E49.bottom"),sQuery(id+"F24.wireOp",EDGE,"E49.top"),sQuery(id+"F24.wireOp",EDGE,"E49.left"),sQuery(id+"F24.wireOp",EDGE,"E49.right")])],"isStart":false});
            var sketch = newSketch(context, id + "F28", { "sketchPlane" : qUnion([Q0])});
            skLineSegment(sketch, "E57", {"start": v(0, 16) * mm, "end": v(0, 9) * mm, "construction": true});
            skLineSegment(sketch, "E58", {"start": v(-117, 12.5) * mm, "end": v(117, 12.5) * mm, "construction": true});
            skLineSegment(sketch, "E59", {"start": v(-100, 16) * mm, "end": v(-100, 9) * mm, "construction": true});
            skLineSegment(sketch, "E60", {"start": v(100, 16) * mm, "end": v(100, 9) * mm, "construction": true});
            skLineSegment(sketch, "E61", {"start": v(-34, 16) * mm, "end": v(-34, 9) * mm, "construction": true});
            skLineSegment(sketch, "E62", {"start": v(34, 16) * mm, "end": v(34, 9) * mm, "construction": true});
            skPoint(sketch, "E63", {"position": v(-100, 12.5) * mm});
            skPoint(sketch, "E64", {"position": v(-34, 12.5) * mm});
            skPoint(sketch, "E65", {"position": v(34, 12.5) * mm});
            skPoint(sketch, "E66", {"position": v(100, 12.5) * mm});
            skSolve(sketch);
        }
        {
            var Q0;
            Q0=sQuery(id+"F28.wireOp",VERTEX,"E65");
            var Q1;
            Q1=sQuery(id+"F28.wireOp",VERTEX,"E64");
            var Q2;
            Q2=sQuery(id+"F28.wireOp",VERTEX,"E63");
            var Q3;
            Q3=sQuery(id+"F28.wireOp",VERTEX,"E66");
            var Q4;
            Q4=makeQuery(id+"F1.opExtrude","SWEPT_BODY",BODY,{"disambiguationData":[OSD([sQuery(id+"F0.wireOp",EDGE,"E0.bottom"),sQuery(id+"F0.wireOp",EDGE,"E0.top"),sQuery(id+"F0.wireOp",EDGE,"E0.left"),sQuery(id+"F0.wireOp",EDGE,"E0.right")])]});
            hole(context, id + "F29", {"style" : HoleStyle.SIMPLE, "endStyle" : HoleEndStyle.BLIND, "holeDiameter" : 5.1 * mm, "majorDiameter" : 5 * mm, "holeDepth" : 8 * mm, "isTappedThrough" : true, "tappedDepth" : 12 * mm, "tapClearance" : 3, "locations" : qUnion([Q0, Q1, Q2, Q3]), "scope" : qUnion([Q4])});
        }
        {
            var Q0;
            {var subQ2=sQuery(id+"F17.wireOp",EDGE,"E41.bottom");Q0=makeQuery(id+"F17.imprint","IMPRINT",FACE,{"disambiguationData":[TD([[makeQuery(id+"F17.imprint","IMPRINT",EDGE,{"derivedFrom":subQ2}),1.0]])]});}
            var Q1;
            {var subQ2=sQuery(id+"F17.wireOp",EDGE,"E43.bottom");Q1=makeQuery(id+"F17.imprint","IMPRINT",FACE,{"disambiguationData":[TD([[makeQuery(id+"F17.imprint","IMPRINT",EDGE,{"derivedFrom":subQ2}),-1.0]])]});}
            var Q2;
            Q2=makeQuery(id+"F1.opExtrude","SWEPT_BODY",BODY,{"disambiguationData":[OSD([sQuery(id+"F0.wireOp",EDGE,"E0.bottom"),sQuery(id+"F0.wireOp",EDGE,"E0.top"),sQuery(id+"F0.wireOp",EDGE,"E0.left"),sQuery(id+"F0.wireOp",EDGE,"E0.right")])]});
            extrude(context, id + "F30", {"entities" : qUnion([Q0, Q1]), "operationType" : NewBodyOperationType.ADD, "oppositeDirection" : true, "depth" : 10 * mm, "endBoundEntityBody" : qUnion([Q2]), "offsetDistance" : 25 * mm});
        }
        {
            var Q0;
            Q0=makeQuery(id+"F30.opExtrude","SWEPT_FACE",FACE,{"disambiguationData":[OSD([sQuery(id+"F17.wireOp",EDGE,"E41.bottom")])]});
            var sketch = newSketch(context, id + "F31", { "sketchPlane" : qUnion([Q0])});
            skLineSegment(sketch, "E67", {"start": v(-52.5, 32.5) * mm, "end": v(-37.5, 42.5) * mm});
            skSolve(sketch);
        }
        {
            var Q0;
            Q0=makeQuery(id+"F31.imprint","IMPRINT",FACE,{"disambiguationData":[TD([[makeQuery(id+"F31.imprint","IMPRINT",EDGE,{"derivedFrom":sQuery(id+"F31.wireOp",EDGE,"E67")}),-1.0]])]});
            var Q1;
            Q1=makeQuery(id+"F30.opExtrude","SWEPT_FACE",FACE,{"disambiguationData":[OSD([sQuery(id+"F17.wireOp",EDGE,"E41.top")])]});
            extrude(context, id + "F32", {"entities" : qUnion([Q0]), "operationType" : NewBodyOperationType.REMOVE, "endBound" : BoundingType.UP_TO_SURFACE, "oppositeDirection" : true, "depth" : 25 * mm, "endBoundEntityFace" : qUnion([Q1]), "offsetDistance" : 25 * mm});
        }
        {
            var Q0;
            Q0=makeQuery(id+"F30.opExtrude","SWEPT_FACE",FACE,{"disambiguationData":[OSD([sQuery(id+"F17.wireOp",EDGE,"E43.bottom")])]});
            var sketch = newSketch(context, id + "F33", { "sketchPlane" : qUnion([Q0])});
            skLineSegment(sketch, "E68", {"start": v(37.5, 42.5) * mm, "end": v(52.5, 32.5) * mm});
            skSolve(sketch);
        }
        {
            var Q0;
            Q0=makeQuery(id+"F33.imprint","IMPRINT",FACE,{"disambiguationData":[TD([[makeQuery(id+"F33.imprint","IMPRINT",EDGE,{"derivedFrom":sQuery(id+"F33.wireOp",EDGE,"E68")}),-1.0]])]});
            var Q1;
            Q1=makeQuery(id+"F30.opExtrude","SWEPT_FACE",FACE,{"disambiguationData":[OSD([sQuery(id+"F17.wireOp",EDGE,"E43.top")])]});
            extrude(context, id + "F34", {"entities" : qUnion([Q0]), "operationType" : NewBodyOperationType.REMOVE, "endBound" : BoundingType.UP_TO_SURFACE, "oppositeDirection" : true, "depth" : 25 * mm, "endBoundEntityFace" : qUnion([Q1]), "offsetDistance" : 25 * mm});
        }
        {
            var Q0;
            Q0=sQuery(id+"F17.wireOp",VERTEX,"E46");
            var Q1;
            Q1=sQuery(id+"F17.wireOp",VERTEX,"E47");
            var Q2;
            Q2=makeQuery(id+"F1.opExtrude","SWEPT_BODY",BODY,{"disambiguationData":[OSD([sQuery(id+"F0.wireOp",EDGE,"E0.bottom"),sQuery(id+"F0.wireOp",EDGE,"E0.top"),sQuery(id+"F0.wireOp",EDGE,"E0.left"),sQuery(id+"F0.wireOp",EDGE,"E0.right")])]});
            hole(context, id + "F35", {"style" : HoleStyle.SIMPLE, "endStyle" : HoleEndStyle.BLIND, "holeDiameter" : 2.5 * mm, "majorDiameter" : 5 * mm, "holeDepth" : 10 * mm, "isTappedThrough" : true, "tappedDepth" : 12 * mm, "tapClearance" : 3, "locations" : qUnion([Q0, Q1]), "scope" : qUnion([Q2])});
        }
        {
            var Q0;
            Q0=makeQuery(id+"F5.opExtrude","CAP_FACE",FACE,{"disambiguationData":[OSD([sQuery(id+"F4.wireOp",EDGE,"E4")])],"isStart":false});
            var sketch = newSketch(context, id + "F36", { "sketchPlane" : qUnion([Q0])});
            skPoint(sketch, "E69", {"position": v(-38, -24.5) * mm});
            skCircle(sketch, "E70.0.0", {"center": v(-40, -52.5) * mm, "radius": 4 * mm});
            skCircle(sketch, "E71.0.0", {"center": v(-40, -110.5) * mm, "radius": 4 * mm});
            skCircle(sketch, "E72.0.0", {"center": v(-38, 110.5) * mm, "radius": 4 * mm});
            skCircle(sketch, "E73.0", {"center": v(38, 110.5) * mm, "radius": 4 * mm});
            skCircle(sketch, "E74.0", {"center": v(38, -24.5) * mm, "radius": 4 * mm});
            skCircle(sketch, "E75.0", {"center": v(40, -52.5) * mm, "radius": 4 * mm});
            skCircle(sketch, "E76.0", {"center": v(40, -110.5) * mm, "radius": 4 * mm});
            skSolve(sketch);
        }
        {
            var Q0;
            Q0=sQuery(id+"F36.wireOp",VERTEX,"E69");
            var Q1;
            Q1=sQuery(id+"F36.wireOp",VERTEX,"E70.0.0.center");
            var Q2;
            Q2=sQuery(id+"F36.wireOp",VERTEX,"E75.0.center");
            var Q3;
            Q3=sQuery(id+"F36.wireOp",VERTEX,"E74.0.center");
            var Q4;
            Q4=sQuery(id+"F36.wireOp",VERTEX,"E71.0.0.center");
            var Q5;
            Q5=sQuery(id+"F36.wireOp",VERTEX,"E73.0.center");
            var Q6;
            Q6=sQuery(id+"F36.wireOp",VERTEX,"E76.0.center");
            var Q7;
            Q7=sQuery(id+"F36.wireOp",VERTEX,"E72.0.0.center");
            var Q8;
            Q8=makeQuery(id+"F1.opExtrude","SWEPT_BODY",BODY,{"disambiguationData":[OSD([sQuery(id+"F0.wireOp",EDGE,"E0.bottom"),sQuery(id+"F0.wireOp",EDGE,"E0.top"),sQuery(id+"F0.wireOp",EDGE,"E0.left"),sQuery(id+"F0.wireOp",EDGE,"E0.right")])]});
            hole(context, id + "F37", {"style" : HoleStyle.SIMPLE, "endStyle" : HoleEndStyle.BLIND, "holeDiameter" : 2.5 * mm, "majorDiameter" : 5 * mm, "holeDepth" : 7 * mm, "isTappedThrough" : true, "tappedDepth" : 12 * mm, "tapClearance" : 3, "startFromSketch" : true, "locations" : qUnion([Q0, Q1, Q2, Q3, Q4, Q5, Q6, Q7]), "scope" : qUnion([Q8])});
        }
    });
